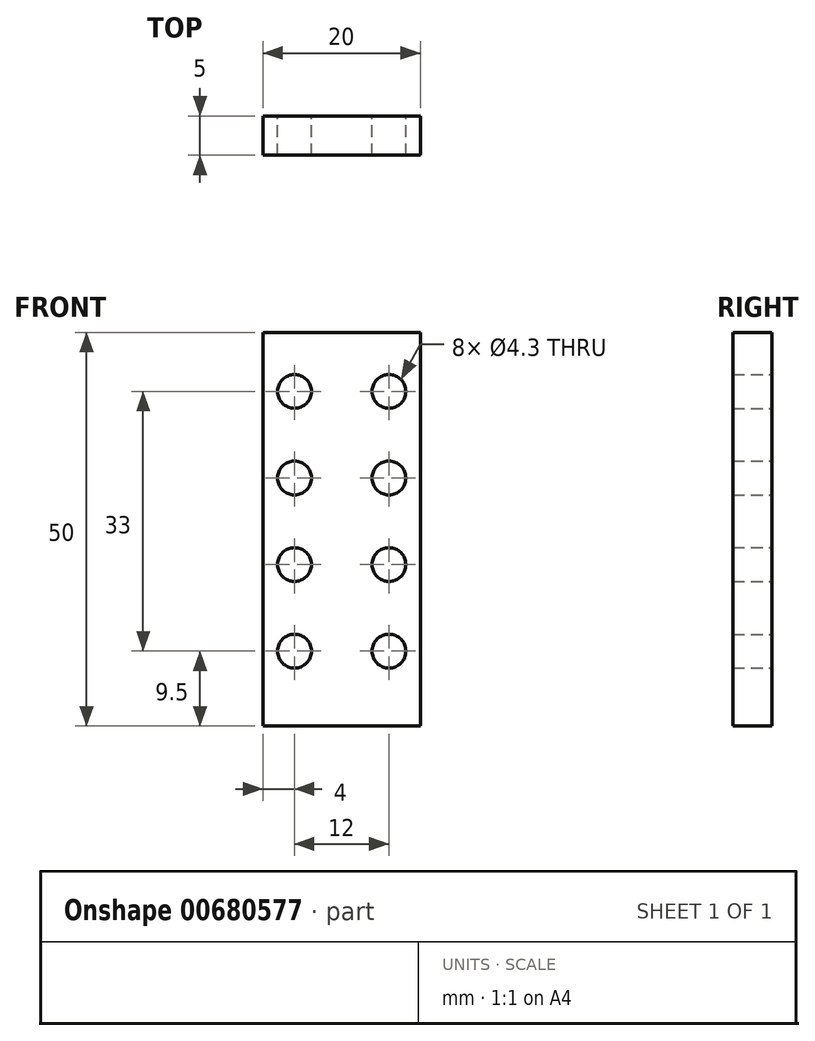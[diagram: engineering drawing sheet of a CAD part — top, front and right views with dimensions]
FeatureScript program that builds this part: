
annotation { "Feature Type Name" : "Feature", "Feature Type Description" : "" }
export const myFeature = defineFeature(function(context is Context, id is Id, definition is map)
    precondition{}
    {
        {
            var Q0;
            Q0=qCreatedBy(makeId("Front.planeOp"),FACE);
            var sketch = newSketch(context, id + "F0", { "sketchPlane" : qUnion([Q0])});
            skLineSegment(sketch, "E0.bottom", {"start": v(10, 25) * mm, "end": v(-10, 25) * mm});
            skLineSegment(sketch, "E0.top", {"start": v(10, -25) * mm, "end": v(-10, -25) * mm});
            skLineSegment(sketch, "E0.left", {"start": v(10, 25) * mm, "end": v(10, -25) * mm});
            skLineSegment(sketch, "E0.right", {"start": v(-10, 25) * mm, "end": v(-10, -25) * mm});
            skPoint(sketch, "E0.middle", {"position": v(0, 0) * mm});
            skLineSegment(sketch, "E1", {"start": v(0, 25) * mm, "end": v(0, -25) * mm, "construction": true});
            skLineSegment(sketch, "E2", {"start": v(-6, 25) * mm, "end": v(-6, -25) * mm, "construction": true});
            skLineSegment(sketch, "E3", {"start": v(-10, 17.5) * mm, "end": v(10, 17.5) * mm, "construction": true});
            skCircle(sketch, "E4", {"center": v(-6, 17.5) * mm, "radius": 2.15 * mm});
            skLineSegment(sketch, "E5", {"start": v(-10, 0) * mm, "end": v(10, 0) * mm, "construction": true});
            skCircle(sketch, "E6.MirrorC", {"center": v(6, 17.5) * mm, "radius": 2.15 * mm});
            skCircle(sketch, "E7.0.1.0", {"center": v(-6, 6.5) * mm, "radius": 2.15 * mm});
            skCircle(sketch, "E7.0.1.1", {"center": v(6, 6.5) * mm, "radius": 2.15 * mm});
            skCircle(sketch, "E7.0.2.0", {"center": v(-6, -4.5) * mm, "radius": 2.15 * mm});
            skCircle(sketch, "E7.0.2.1", {"center": v(6, -4.5) * mm, "radius": 2.15 * mm});
            skCircle(sketch, "E7.0.3.0", {"center": v(-6, -15.5) * mm, "radius": 2.15 * mm});
            skCircle(sketch, "E7.0.3.1", {"center": v(6, -15.5) * mm, "radius": 2.15 * mm});
            skLineSegment(sketch, "E7.direction1", {"start": v(-6, 17.5) * mm, "end": v(19, 17.5) * mm, "construction": true});
            skLineSegment(sketch, "E7.direction2", {"start": v(-6, 17.5) * mm, "end": v(-6, 6.5) * mm, "construction": true});
            skSolve(sketch);
        }
        {
            var Q0;
            Q0 = qSketchRegion(id + "F0", true);
            extrude(context, id + "F1", {"entities" : qUnion([Q0]), "depth" : 5 * mm, "offsetDistance" : 25 * mm});
        }
    });
